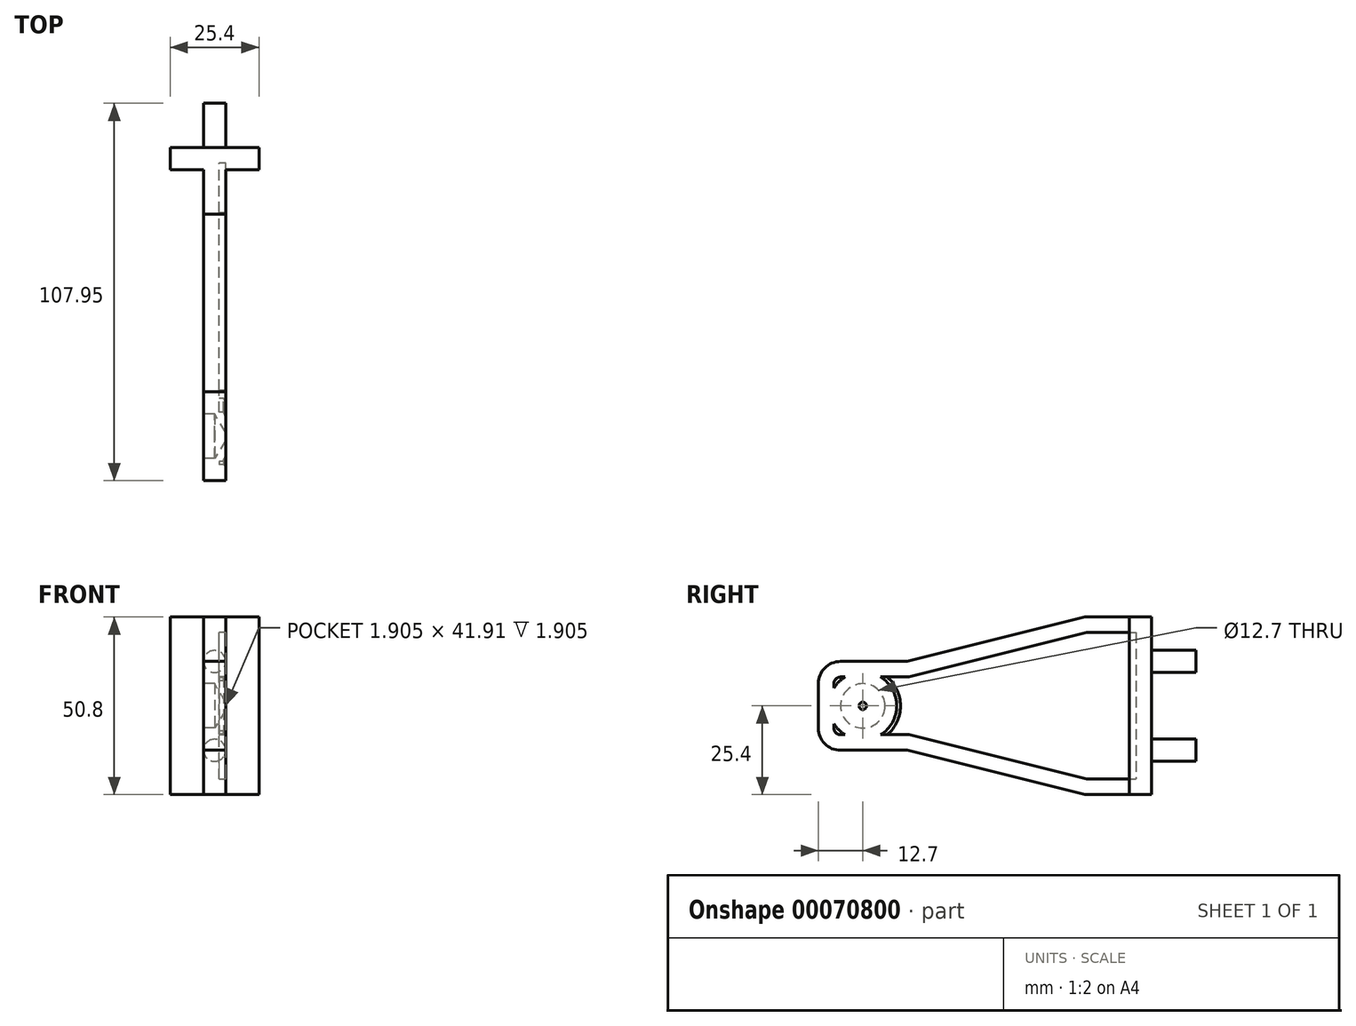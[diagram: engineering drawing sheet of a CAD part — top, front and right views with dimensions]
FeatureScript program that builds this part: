
annotation { "Feature Type Name" : "Feature", "Feature Type Description" : "" }
export const myFeature = defineFeature(function(context is Context, id is Id, definition is map)
    precondition{}
    {
        {
            var Q0;
            Q0=qCreatedBy(makeId("Front.planeOp"),FACE);
            var sketch = newSketch(context, id + "F0", { "sketchPlane" : qUnion([Q0])});
            skLineSegment(sketch, "E0.bottom", {"start": v(0, 0) * mm, "end": v(-25.4, 0) * mm});
            skLineSegment(sketch, "E0.top", {"start": v(0, 50.8) * mm, "end": v(-25.4, 50.8) * mm});
            skLineSegment(sketch, "E0.left", {"start": v(0, 0) * mm, "end": v(0, 50.8) * mm});
            skLineSegment(sketch, "E0.right", {"start": v(-25.4, 0) * mm, "end": v(-25.4, 50.8) * mm});
            skSolve(sketch);
        }
        {
            var Q0;
            Q0=makeQuery(id+"F0.imprint","IMPRINT",FACE,{"disambiguationData":[TD([[makeQuery(id+"F0.imprint","IMPRINT",EDGE,{"derivedFrom":sQuery(id+"F0.wireOp",EDGE,"E0.bottom")}),-1.0]])]});
            extrude(context, id + "F1", {"entities" : qUnion([Q0]), "depth" : 6.35 * mm});
        }
        {
            var Q0;
            Q0=makeQuery(id+"F1.opExtrude","CAP_FACE",FACE,{"disambiguationData":[OSD([sQuery(id+"F0.wireOp",EDGE,"E0.bottom"),sQuery(id+"F0.wireOp",EDGE,"E0.top"),sQuery(id+"F0.wireOp",EDGE,"E0.left"),sQuery(id+"F0.wireOp",EDGE,"E0.right")])],"isStart":false});
            var sketch = newSketch(context, id + "F2", { "sketchPlane" : qUnion([Q0])});
            skLineSegment(sketch, "E1.bottom", {"start": v(-15.87, 0) * mm, "end": v(-9.52, 0) * mm});
            skLineSegment(sketch, "E1.top", {"start": v(-15.88, 50.8) * mm, "end": v(-9.53, 50.8) * mm});
            skLineSegment(sketch, "E1.left", {"start": v(-15.87, 0) * mm, "end": v(-15.88, 50.8) * mm});
            skLineSegment(sketch, "E1.right", {"start": v(-9.52, 0) * mm, "end": v(-9.53, 50.8) * mm});
            skSolve(sketch);
        }
        {
            var Q0;
            Q0=makeQuery(id+"F2.imprint","IMPRINT",FACE,{"disambiguationData":[TD([[makeQuery(id+"F2.imprint","IMPRINT",EDGE,{"derivedFrom":sQuery(id+"F2.wireOp",EDGE,"E1.bottom")}),-1.0]])]});
            extrude(context, id + "F3", {"entities" : qUnion([Q0]), "operationType" : NewBodyOperationType.ADD, "depth" : 12.7 * mm});
        }
        {
            var Q0;
            Q0=makeQuery(id+"F3.opExtrude","CAP_FACE",FACE,{"disambiguationData":[OSD([sQuery(id+"F2.wireOp",EDGE,"E1.bottom"),sQuery(id+"F2.wireOp",EDGE,"E1.top"),sQuery(id+"F2.wireOp",EDGE,"E1.left"),sQuery(id+"F2.wireOp",EDGE,"E1.right")])],"isStart":false});
            cPlane(context, id + "F4", {"entities" : qUnion([Q0]), "cplaneType" : CPlaneType.OFFSET, "offset" : 50.8 * mm, "width" : 152.4 * mm, "height" : 152.4 * mm});
        }
        {
            var Q0;
            Q0=qCreatedBy(id+"F4.planeOp",FACE);
            var sketch = newSketch(context, id + "F5", { "sketchPlane" : qUnion([Q0])});
            skLineSegment(sketch, "E2", {"start": v(-15.88, 38.1) * mm, "end": v(-9.53, 38.1) * mm});
            skLineSegment(sketch, "E3", {"start": v(-15.87, 12.7) * mm, "end": v(-9.52, 12.7) * mm});
            skLineSegment(sketch, "E4", {"start": v(-15.88, 38.1) * mm, "end": v(-15.87, 12.7) * mm});
            skLineSegment(sketch, "E5", {"start": v(-9.53, 38.1) * mm, "end": v(-9.52, 12.7) * mm});
            skSolve(sketch);
        }
        {
            var Q1;
            Q1=makeQuery(id+"F5.imprint","IMPRINT",FACE,{"disambiguationData":[TD([[makeQuery(id+"F5.imprint","IMPRINT",EDGE,{"derivedFrom":sQuery(id+"F5.wireOp",EDGE,"E2")}),-1.0]])]});
            var Q2;
            Q2=makeQuery(id+"F3.opExtrude","CAP_FACE",FACE,{"disambiguationData":[OSD([sQuery(id+"F2.wireOp",EDGE,"E1.bottom"),sQuery(id+"F2.wireOp",EDGE,"E1.top"),sQuery(id+"F2.wireOp",EDGE,"E1.left"),sQuery(id+"F2.wireOp",EDGE,"E1.right")])],"isStart":false});
            loft(context, id + "F6", {"operationType" : NewBodyOperationType.ADD, "sheetProfilesArray" : [{ "sheetProfileEntities" : qUnion([Q1]) }, { "sheetProfileEntities" : qUnion([Q2]) }]});
        }
        {
            var Q0;
            Q0=makeQuery(id+"F6.opLoft","CAP_FACE",FACE,{"disambiguationData":[OSD([makeQuery(id+"F5.imprint","IMPRINT",FACE,{"disambiguationData":[TD([[makeQuery(id+"F5.imprint","IMPRINT",EDGE,{"derivedFrom":sQuery(id+"F5.wireOp",EDGE,"E2")}),-1.0]])]})])],"isStart":true});
            extrude(context, id + "F7", {"entities" : qUnion([Q0]), "operationType" : NewBodyOperationType.ADD, "depth" : 25.4 * mm});
        }
        {
            var Q0;
            Q0=makeQuery(id+"F7.opExtrude","CAP_EDGE",EDGE,{"disambiguationData":[OSD([sQuery(id+"F5.wireOp",EDGE,"E3"),sQuery(id+"F5.wireOp",EDGE,"E4"),sQuery(id+"F5.wireOp",EDGE,"E5")])],"isStart":false});
            var Q1;
            Q1=makeQuery(id+"F7.opExtrude","CAP_EDGE",EDGE,{"disambiguationData":[OSD([sQuery(id+"F5.wireOp",EDGE,"E2"),sQuery(id+"F5.wireOp",EDGE,"E4"),sQuery(id+"F5.wireOp",EDGE,"E5")])],"isStart":false});
            fillet(context, id + "F8", {"entities" : qUnion([Q0, Q1]), "radius" : 6.35 * mm, "tangentPropagation" : true, "allowEdgeOverflow" : false});
        }
        {
            var Q0;
            {var subQ0=sQuery(id+"F5.wireOp",EDGE,"E4");var subQ1=sQuery(id+"F5.wireOp",EDGE,"E3");var subQ2=sQuery(id+"F5.wireOp",EDGE,"E2");var subQ3=sQuery(id+"F2.wireOp",EDGE,"E1.left");Q0=makeQuery(id+"F7.boolean.opBoolean","MERGE",FACE,{"derivedFrom":[makeQuery(id+"F6.boolean.opBoolean","MERGE",FACE,{"derivedFrom":[makeQuery(id+"F3.opExtrude","SWEPT_FACE",FACE,{"disambiguationData":[OSD([subQ3])]}),makeQuery(id+"F6.opLoft","SWEPT_FACE",FACE,{"disambiguationData":[OSD([sQuery(id+"F0.wireOp",EDGE,"E0.bottom"),sQuery(id+"F0.wireOp",EDGE,"E0.top"),sQuery(id+"F2.wireOp",EDGE,"E1.bottom"),sQuery(id+"F2.wireOp",EDGE,"E1.top"),subQ3,subQ2,subQ1,subQ0])]})]}),makeQuery(id+"F7.opExtrude","SWEPT_FACE",FACE,{"disambiguationData":[OSD([subQ2,subQ1,subQ0])]})]});}
            var sketch = newSketch(context, id + "F9", { "sketchPlane" : qUnion([Q0])});
            skPoint(sketch, "E6", {"position": v(82.55, 25.4) * mm});
            skPoint(sketch, "E6.positionSnap0", {"position": v(95.25, 25.4) * mm});
            skSolve(sketch);
        }
        {
            var Q0;
            Q0=sQuery(id+"F9.wireOp",VERTEX,"E6");
            var Q1;
            Q1=makeQuery(id+"F1.opExtrude","SWEPT_BODY",BODY,{"disambiguationData":[OSD([sQuery(id+"F0.wireOp",EDGE,"E0.bottom"),sQuery(id+"F0.wireOp",EDGE,"E0.top"),sQuery(id+"F0.wireOp",EDGE,"E0.left"),sQuery(id+"F0.wireOp",EDGE,"E0.right")])]});
            hole(context, id + "F10", {"style" : HoleStyle.SIMPLE, "endStyle" : HoleEndStyle.BLIND, "holeDiameter" : 12.7 * mm, "holeDepth" : 3.17 * mm, "locations" : qUnion([Q0]), "scope" : qUnion([Q1])});
        }
        {
            var Q0;
            Q0=makeQuery(id+"F1.opExtrude","CAP_FACE",FACE,{"disambiguationData":[OSD([sQuery(id+"F0.wireOp",EDGE,"E0.bottom"),sQuery(id+"F0.wireOp",EDGE,"E0.top"),sQuery(id+"F0.wireOp",EDGE,"E0.left"),sQuery(id+"F0.wireOp",EDGE,"E0.right")])],"isStart":true});
            var sketch = newSketch(context, id + "F11", { "sketchPlane" : qUnion([Q0])});
            skCircle(sketch, "E7", {"center": v(12.7, 38.1) * mm, "radius": 3.18 * mm});
            skPoint(sketch, "E7.centerSnap0", {"position": v(12.7, 50.8) * mm});
            skCircle(sketch, "E8", {"center": v(12.7, 12.7) * mm, "radius": 3.18 * mm});
            skPoint(sketch, "E8.centerSnap0", {"position": v(12.7, 0) * mm});
            skSolve(sketch);
        }
        {
            var Q0;
            Q0=makeQuery(id+"F11.imprint","IMPRINT",FACE,{"disambiguationData":[TD([[makeQuery(id+"F11.imprint","IMPRINT",EDGE,{"derivedFrom":sQuery(id+"F11.wireOp",EDGE,"E7")}),1.0]])]});
            var Q1;
            Q1=makeQuery(id+"F11.imprint","IMPRINT",FACE,{"disambiguationData":[TD([[makeQuery(id+"F11.imprint","IMPRINT",EDGE,{"derivedFrom":sQuery(id+"F11.wireOp",EDGE,"E8")}),1.0]])]});
            extrude(context, id + "F12", {"entities" : qUnion([Q0, Q1]), "operationType" : NewBodyOperationType.ADD, "depth" : 12.7 * mm});
        }
        {
            var Q0;
            {var subQ0=sQuery(id+"F5.wireOp",EDGE,"E5");var subQ1=sQuery(id+"F5.wireOp",EDGE,"E3");var subQ2=sQuery(id+"F5.wireOp",EDGE,"E2");var subQ3=sQuery(id+"F2.wireOp",EDGE,"E1.right");Q0=makeQuery(id+"F7.boolean.opBoolean","MERGE",FACE,{"derivedFrom":[makeQuery(id+"F6.boolean.opBoolean","MERGE",FACE,{"derivedFrom":[makeQuery(id+"F3.opExtrude","SWEPT_FACE",FACE,{"disambiguationData":[OSD([subQ3])]}),makeQuery(id+"F6.opLoft","SWEPT_FACE",FACE,{"disambiguationData":[OSD([sQuery(id+"F0.wireOp",EDGE,"E0.bottom"),sQuery(id+"F0.wireOp",EDGE,"E0.top"),sQuery(id+"F2.wireOp",EDGE,"E1.bottom"),sQuery(id+"F2.wireOp",EDGE,"E1.top"),subQ3,subQ2,subQ1,subQ0])]})]}),makeQuery(id+"F7.opExtrude","SWEPT_FACE",FACE,{"disambiguationData":[OSD([subQ2,subQ1,subQ0])]})]});}
            shell(context, id + "F13", {"entities" : qUnion([Q0]), "thickness" : 4.44 * mm});
        }
    });
